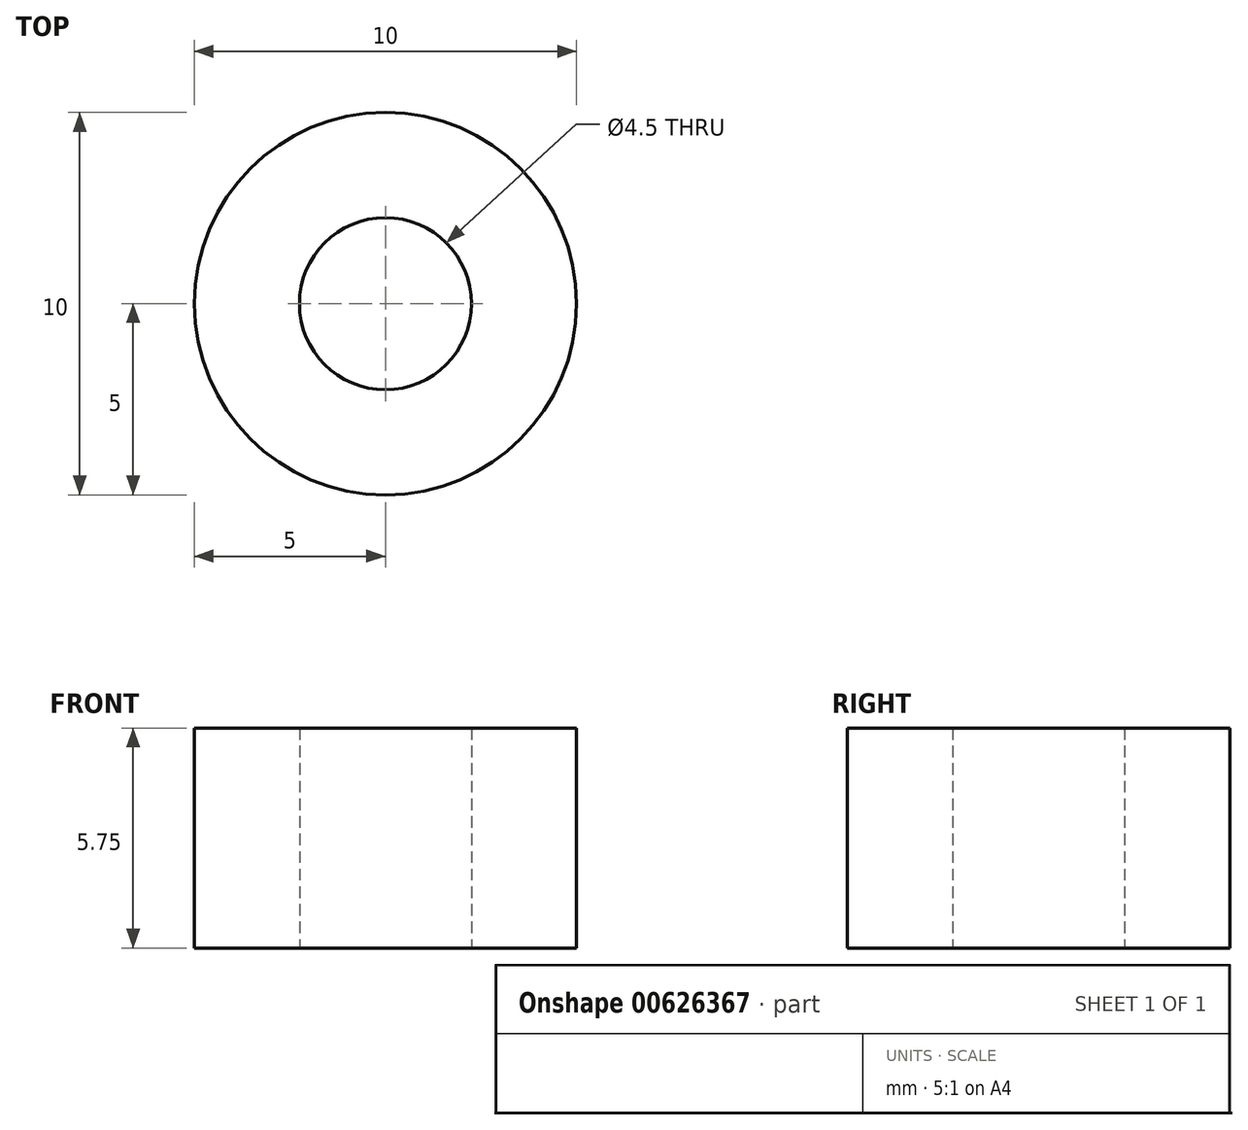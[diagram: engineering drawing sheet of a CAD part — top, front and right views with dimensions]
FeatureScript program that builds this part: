
annotation { "Feature Type Name" : "Feature", "Feature Type Description" : "" }
export const myFeature = defineFeature(function(context is Context, id is Id, definition is map)
    precondition{}
    {
        {
            var Q0;
            Q0=qCreatedBy(makeId("Top.planeOp"),FACE);
            var sketch = newSketch(context, id + "F0", { "sketchPlane" : qUnion([Q0])});
            skCircle(sketch, "E0", {"center": v(0, 0) * mm, "radius": 5 * mm});
            skCircle(sketch, "E1", {"center": v(0, 0) * mm, "radius": 2.25 * mm});
            skSolve(sketch);
        }
        {
            var Q0;
            Q0 = qSketchRegion(id + "F0", true);
            extrude(context, id + "F1", {"entities" : qUnion([Q0]), "depth" : 5.75 * mm, "offsetDistance" : 25 * mm});
        }
    });
